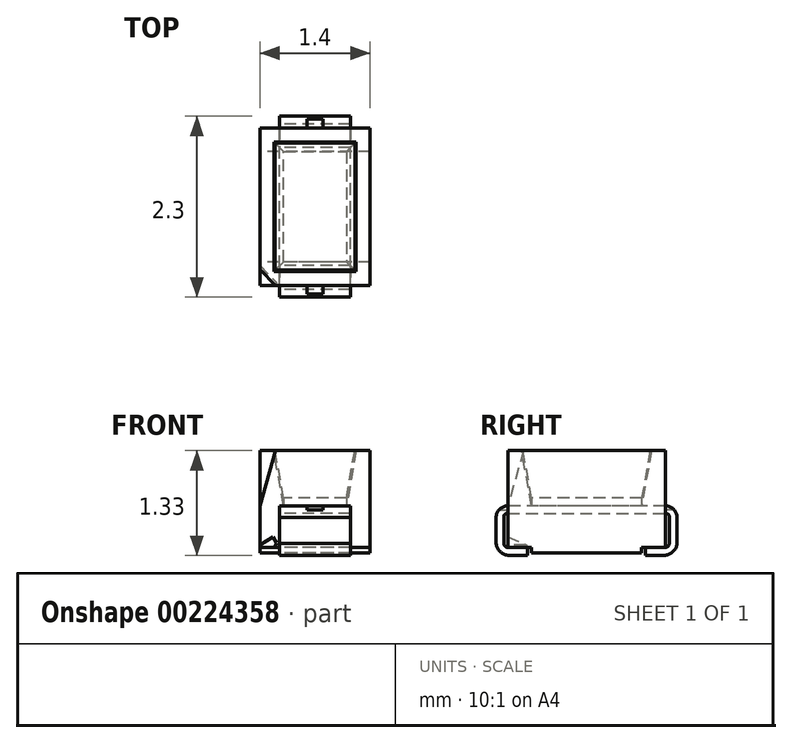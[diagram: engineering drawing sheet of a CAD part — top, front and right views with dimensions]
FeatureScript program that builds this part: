
annotation { "Feature Type Name" : "Feature", "Feature Type Description" : "" }
export const myFeature = defineFeature(function(context is Context, id is Id, definition is map)
    precondition{}
    {
        {
            var Q0;
            Q0=qCreatedBy(makeId("Top.planeOp"),FACE);
            var sketch = newSketch(context, id + "F0", { "sketchPlane" : qUnion([Q0])});
            skLineSegment(sketch, "E0.bottom", {"start": v(0.7, -1) * mm, "end": v(-0.7, -1) * mm});
            skLineSegment(sketch, "E0.top", {"start": v(0.7, 1) * mm, "end": v(-0.7, 1) * mm});
            skLineSegment(sketch, "E0.left", {"start": v(0.7, -1) * mm, "end": v(0.7, 1) * mm});
            skLineSegment(sketch, "E0.right", {"start": v(-0.7, -1) * mm, "end": v(-0.7, 1) * mm});
            skPoint(sketch, "E0.middle", {"position": v(0, 0) * mm});
            skLineSegment(sketch, "E1.bottom", {"start": v(0.4, -0.7) * mm, "end": v(-0.4, -0.7) * mm});
            skLineSegment(sketch, "E1.top", {"start": v(0.4, 0.7) * mm, "end": v(-0.4, 0.7) * mm});
            skLineSegment(sketch, "E1.left", {"start": v(0.4, -0.7) * mm, "end": v(0.4, 0.7) * mm});
            skLineSegment(sketch, "E1.right", {"start": v(-0.4, -0.7) * mm, "end": v(-0.4, 0.7) * mm});
            skLineSegment(sketch, "E2.bottom", {"start": v(0.15, -0.4) * mm, "end": v(-0.15, -0.4) * mm});
            skLineSegment(sketch, "E2.top", {"start": v(0.15, -0.1) * mm, "end": v(-0.15, -0.1) * mm});
            skLineSegment(sketch, "E2.left", {"start": v(0.15, -0.4) * mm, "end": v(0.15, -0.1) * mm});
            skLineSegment(sketch, "E2.right", {"start": v(-0.15, -0.4) * mm, "end": v(-0.15, -0.1) * mm});
            skPoint(sketch, "E2.middle", {"position": v(0, -0.25) * mm});
            skSolve(sketch);
        }
        {
            var Q0;
            Q0=makeQuery(id+"F0.imprint","IMPRINT",FACE,{"disambiguationData":[TD([[makeQuery(id+"F0.imprint","IMPRINT",EDGE,{"derivedFrom":sQuery(id+"F0.wireOp",EDGE,"E0.bottom")}),-1.0]])]});
            var Q1;
            {var subQ1=sQuery(id+"F0.wireOp",EDGE,"E0.top");Q1=makeQuery(id+"F0.imprint","IMPRINT",FACE,{"disambiguationData":[TD([[makeQuery(id+"F0.imprint","IMPRINT",EDGE,{"derivedFrom":subQ1}),1.0]])]});}
            extrude(context, id + "F1", {"entities" : qUnion([Q0, Q1]), "depth" : .7 * mm, "hasSecondDirection" : true, "secondDirectionOppositeDirection" : true, "secondDirectionDepth" : .6 * mm});
        }
        {
            var Q0;
            Q0=makeQuery(id+"F0.imprint","IMPRINT",FACE,{"disambiguationData":[TD([[makeQuery(id+"F0.imprint","IMPRINT",EDGE,{"derivedFrom":sQuery(id+"F0.wireOp",EDGE,"E1.bottom")}),-1.0]])]});
            var Q1;
            Q1=makeQuery(id+"F1.opExtrude","CAP_FACE",FACE,{"disambiguationData":[OSD([sQuery(id+"F0.wireOp",EDGE,"E0.bottom"),sQuery(id+"F0.wireOp",EDGE,"E0.top"),sQuery(id+"F0.wireOp",EDGE,"E0.left"),sQuery(id+"F0.wireOp",EDGE,"E0.right"),sQuery(id+"F0.wireOp",EDGE,"E1.bottom"),sQuery(id+"F0.wireOp",EDGE,"E1.top"),sQuery(id+"F0.wireOp",EDGE,"E1.left"),sQuery(id+"F0.wireOp",EDGE,"E1.right")])],"isStart":false});
            extrude(context, id + "F2", {"entities" : qUnion([Q0]), "operationType" : NewBodyOperationType.REMOVE, "endBound" : BoundingType.UP_TO_SURFACE, "endBoundEntityFace" : qUnion([Q1]), "depth" : 25 * mm, "hasDraft" : true, "draftAngle" : 10 * degree});
        }
        {
            var Q0;
            Q0=makeQuery(id+"F0.imprint","IMPRINT",FACE,{"disambiguationData":[TD([[makeQuery(id+"F0.imprint","IMPRINT",EDGE,{"derivedFrom":sQuery(id+"F0.wireOp",EDGE,"E2.bottom")}),-1.0]])]});
            extrude(context, id + "F3", {"entities" : qUnion([Q0]), "depth" : .1 * mm});
        }
        {
            var Q0;
            Q0=makeQuery(id+"F0.imprint","IMPRINT",FACE,{"disambiguationData":[TD([[makeQuery(id+"F0.imprint","IMPRINT",EDGE,{"derivedFrom":sQuery(id+"F0.wireOp",EDGE,"E1.bottom")}),-1.0]])]});
            var Q1;
            Q1=makeQuery(id+"F1.opExtrude","CAP_FACE",FACE,{"disambiguationData":[OSD([sQuery(id+"F0.wireOp",EDGE,"E0.bottom"),sQuery(id+"F0.wireOp",EDGE,"E0.top"),sQuery(id+"F0.wireOp",EDGE,"E0.left"),sQuery(id+"F0.wireOp",EDGE,"E0.right"),sQuery(id+"F0.wireOp",EDGE,"E1.bottom"),sQuery(id+"F0.wireOp",EDGE,"E1.top"),sQuery(id+"F0.wireOp",EDGE,"E1.left"),sQuery(id+"F0.wireOp",EDGE,"E1.right")])],"isStart":true});
            extrude(context, id + "F4", {"entities" : qUnion([Q0]), "operationType" : NewBodyOperationType.ADD, "endBound" : BoundingType.UP_TO_SURFACE, "oppositeDirection" : true, "endBoundEntityFace" : qUnion([Q1]), "depth" : 25 * mm});
        }
        {
            var Q0;
            Q0=makeQuery(id+"F0.imprint","IMPRINT",FACE,{"disambiguationData":[TD([[makeQuery(id+"F0.imprint","IMPRINT",EDGE,{"derivedFrom":sQuery(id+"F0.wireOp",EDGE,"E1.bottom")}),-1.0]])]});
            extrude(context, id + "F5", {"entities" : qUnion([Q0]), "depth" : .1 * mm});
        }
        {
            var Q0;
            Q0=makeQuery(id+"F0.imprint","IMPRINT",FACE,{"disambiguationData":[TD([[makeQuery(id+"F0.imprint","IMPRINT",EDGE,{"derivedFrom":sQuery(id+"F0.wireOp",EDGE,"E2.bottom")}),-1.0]])]});
            var Q1;
            {var subQ0=sQuery(id+"F0.wireOp",EDGE,"E1.right");var subQ1=sQuery(id+"F0.wireOp",EDGE,"E1.left");var subQ2=sQuery(id+"F0.wireOp",EDGE,"E1.top");var subQ3=sQuery(id+"F0.wireOp",EDGE,"E1.bottom");var subQ4=sQuery(id+"F0.wireOp",EDGE,"E0.right");var subQ5=sQuery(id+"F0.wireOp",EDGE,"E0.left");var subQ6=sQuery(id+"F0.wireOp",EDGE,"E0.top");var subQ7=sQuery(id+"F0.wireOp",EDGE,"E0.bottom");Q1=makeQuery(id+"F4.boolean.opBoolean","MERGE",FACE,{"derivedFrom":[makeQuery(id+"F1.opExtrude","CAP_FACE",FACE,{"disambiguationData":[OSD([subQ7,subQ6,subQ5,subQ4,subQ3,subQ2,subQ1,subQ0])],"isStart":true}),makeQuery(id+"F4.opExtrude","CAP_FACE",FACE,{"disambiguationData":[OSD([subQ7,subQ6,subQ5,subQ4,subQ3,subQ2,subQ1,subQ0])],"isStart":false})]});}
            extrude(context, id + "F6", {"entities" : qUnion([Q0]), "operationType" : NewBodyOperationType.ADD, "endBound" : BoundingType.UP_TO_SURFACE, "oppositeDirection" : true, "endBoundEntityFace" : qUnion([Q1]), "depth" : 25 * mm});
        }
        {
            var Q0;
            Q0=makeQuery(id+"F1.opExtrude","SWEPT_FACE",FACE,{"disambiguationData":[OSD([sQuery(id+"F0.wireOp",EDGE,"E0.right")])]});
            var sketch = newSketch(context, id + "F7", { "sketchPlane" : qUnion([Q0])});
            skLineSegment(sketch, "E3", {"start": v(-1, 0.7) * mm, "end": v(1, 0.7) * mm, "construction": true});
            skLineSegment(sketch, "E4", {"start": v(1, 0.7) * mm, "end": v(1, -0.6) * mm, "construction": true});
            skLineSegment(sketch, "E5", {"start": v(1, -0.6) * mm, "end": v(-1, -0.6) * mm, "construction": true});
            skLineSegment(sketch, "E6", {"start": v(-1, -0.6) * mm, "end": v(-1, 0.7) * mm, "construction": true});
            skLineSegment(sketch, "E7", {"start": v(-1.16, -0.53) * mm, "end": v(-0.7, -0.53) * mm});
            skLineSegment(sketch, "E8", {"start": v(-0.7, -0.53) * mm, "end": v(-0.7, -0.74) * mm});
            skLineSegment(sketch, "E9", {"start": v(-0.7, -0.74) * mm, "end": v(0.7, -0.74) * mm});
            skLineSegment(sketch, "E10", {"start": v(0.7, -0.74) * mm, "end": v(0.7, -0.53) * mm});
            skLineSegment(sketch, "E11", {"start": v(0.7, -0.53) * mm, "end": v(1.16, -0.53) * mm});
            skLineSegment(sketch, "E12", {"start": v(1.16, -0.53) * mm, "end": v(1.16, -0.97) * mm});
            skLineSegment(sketch, "E13", {"start": v(1.16, -0.97) * mm, "end": v(-1.16, -0.97) * mm});
            skLineSegment(sketch, "E14", {"start": v(-1.16, -0.97) * mm, "end": v(-1.16, -0.53) * mm});
            skSolve(sketch);
        }
        {
            var Q0;
            {var subQ0=sQuery(id+"F7.wireOp",EDGE,"E8");var subQ1=sQuery(id+"F7.wireOp",EDGE,"E7");var subQ2=makeQuery(id+"F7.imprint","INTERSECT",VERTEX,{"derivedFrom":[subQ1,subQ0]});Q0=makeQuery(id+"F7.imprint","IMPRINT",FACE,{"disambiguationData":[TD([[makeQuery(id+"F7.imprint","IMPRINT",EDGE,{"disambiguationData":[TD([[subQ2,-1.0]])],"derivedFrom":subQ0}),-1.0]])]});}
            var Q1;
            {var subQ0=sQuery(id+"F7.wireOp",EDGE,"E11");var subQ1=sQuery(id+"F7.wireOp",EDGE,"E10");var subQ2=makeQuery(id+"F7.imprint","INTERSECT",VERTEX,{"derivedFrom":[subQ1,subQ0]});Q1=makeQuery(id+"F7.imprint","IMPRINT",FACE,{"disambiguationData":[TD([[makeQuery(id+"F7.imprint","IMPRINT",EDGE,{"disambiguationData":[TD([[subQ2,1.0]])],"derivedFrom":subQ1}),-1.0]])]});}
            extrude(context, id + "F8", {"entities" : qUnion([Q0, Q1]), "operationType" : NewBodyOperationType.REMOVE, "endBound" : BoundingType.UP_TO_NEXT, "oppositeDirection" : true, "depth" : 25 * mm});
        }
        {
            var Q0;
            Q0=makeQuery(id+"F1.opExtrude","SWEPT_FACE",FACE,{"disambiguationData":[OSD([sQuery(id+"F0.wireOp",EDGE,"E0.right")])]});
            var sketch = newSketch(context, id + "F9", { "sketchPlane" : qUnion([Q0])});
            skLineSegment(sketch, "E15", {"start": v(-1, 0) * mm, "end": v(1, 0) * mm, "construction": true});
            skLineSegment(sketch, "E16", {"start": v(-1.15, -0.15) * mm, "end": v(-1.15, -0.48) * mm});
            skLineSegment(sketch, "E17", {"start": v(-1, -0.63) * mm, "end": v(-0.75, -0.63) * mm});
            skLineSegment(sketch, "E18", {"start": v(-1.15, 0) * mm, "end": v(1.15, 0) * mm});
            skLineSegment(sketch, "E19", {"start": v(1.15, -0.15) * mm, "end": v(1.15, -0.48) * mm});
            skLineSegment(sketch, "E20", {"start": v(1, -0.63) * mm, "end": v(0.75, -0.63) * mm});
            skLineSegment(sketch, "E21", {"start": v(0.75, -0.63) * mm, "end": v(0.75, -0.53) * mm});
            skLineSegment(sketch, "E22", {"start": v(0.75, -0.53) * mm, "end": v(1, -0.53) * mm});
            skLineSegment(sketch, "E23", {"start": v(1.05, -0.48) * mm, "end": v(1.05, -0.15) * mm});
            skLineSegment(sketch, "E24", {"start": v(1, -0.1) * mm, "end": v(-1, -0.1) * mm});
            skLineSegment(sketch, "E25", {"start": v(-1.05, -0.15) * mm, "end": v(-1.05, -0.48) * mm});
            skLineSegment(sketch, "E26", {"start": v(-1, -0.53) * mm, "end": v(-0.75, -0.53) * mm});
            skLineSegment(sketch, "E27", {"start": v(-0.75, -0.53) * mm, "end": v(-0.75, -0.63) * mm});
            skPoint(sketch, "E28.visualSharp", {"position": v(-1.05, -0.1) * mm});
            skArc(sketch, "E28.filletArc", {"start": v(-1, -0.1) * mm, "mid": v(-1.04, -0.11) * mm, "end": v(-1.05, -0.15) * mm});
            skPoint(sketch, "E29.newPointA", {"position": v(0, 0) * mm});
            skArc(sketch, "E29.filletArc", {"start": v(-1, 0) * mm, "mid": v(-1.1, -0.04) * mm, "end": v(-1.15, -0.15) * mm});
            skPoint(sketch, "E30.visualSharp", {"position": v(-1.15, -0.63) * mm});
            skArc(sketch, "E30.filletArc", {"start": v(-1.15, -0.48) * mm, "mid": v(-1.1, -0.58) * mm, "end": v(-1, -0.63) * mm});
            skPoint(sketch, "E31.visualSharp", {"position": v(-1.05, -0.53) * mm});
            skArc(sketch, "E31.filletArc", {"start": v(-1.05, -0.48) * mm, "mid": v(-1.04, -0.51) * mm, "end": v(-1, -0.53) * mm});
            skPoint(sketch, "E32.visualSharp", {"position": v(1.05, -0.53) * mm});
            skArc(sketch, "E32.filletArc", {"start": v(1, -0.53) * mm, "mid": v(1.04, -0.51) * mm, "end": v(1.05, -0.48) * mm});
            skPoint(sketch, "E33.visualSharp", {"position": v(1.05, -0.1) * mm});
            skArc(sketch, "E33.filletArc", {"start": v(1.05, -0.15) * mm, "mid": v(1.04, -0.11) * mm, "end": v(1, -0.1) * mm});
            skArc(sketch, "E34.filletArc", {"start": v(1.15, -0.15) * mm, "mid": v(1.1, -0.04) * mm, "end": v(1, 0) * mm});
            skPoint(sketch, "E35.visualSharp", {"position": v(1.15, -0.63) * mm});
            skArc(sketch, "E35.filletArc", {"start": v(1, -0.63) * mm, "mid": v(1.1, -0.58) * mm, "end": v(1.15, -0.48) * mm});
            skSolve(sketch);
        }
        {
            var Q0;
            Q0 = qSketchRegion(id + "F9", true);
            var Q1;
            Q1=makeQuery(id+"F1.opExtrude","SWEPT_FACE",FACE,{"disambiguationData":[OSD([sQuery(id+"F0.wireOp",EDGE,"E0.left")])]});
            extrude(context, id + "F10", {"entities" : qUnion([Q0]), "oppositeDirection" : true, "endBoundEntityFace" : qUnion([Q1]), "depth" : 1.15 * mm, "hasSecondDirection" : true, "secondDirectionOppositeDirection" : true, "secondDirectionDepth" : .25 * mm});
        }
        {
            var Q0;
            Q0=makeQuery(id+"F5.opExtrude","CAP_FACE",FACE,{"disambiguationData":[OSD([sQuery(id+"F0.wireOp",EDGE,"E1.bottom"),sQuery(id+"F0.wireOp",EDGE,"E1.top"),sQuery(id+"F0.wireOp",EDGE,"E1.left"),sQuery(id+"F0.wireOp",EDGE,"E1.right"),sQuery(id+"F0.wireOp",EDGE,"E2.bottom"),sQuery(id+"F0.wireOp",EDGE,"E2.top"),sQuery(id+"F0.wireOp",EDGE,"E2.left"),sQuery(id+"F0.wireOp",EDGE,"E2.right")])],"isStart":false});
            var sketch = newSketch(context, id + "F11", { "sketchPlane" : qUnion([Q0])});
            skLineSegment(sketch, "E36.0.1", {"start": v(-0.45, 1) * mm, "end": v(0.45, 1) * mm});
            skLineSegment(sketch, "E37", {"start": v(0, 1) * mm, "end": v(0.1, 1) * mm});
            skLineSegment(sketch, "E38", {"start": v(0.1, 1) * mm, "end": v(0.1, 1.2) * mm});
            skLineSegment(sketch, "E39", {"start": v(0.1, 1.2) * mm, "end": v(-0.1, 1.2) * mm});
            skLineSegment(sketch, "E40", {"start": v(-0.1, 1.2) * mm, "end": v(-0.1, 1) * mm});
            skLineSegment(sketch, "E41", {"start": v(-0.1, 1) * mm, "end": v(0, 1) * mm});
            skPoint(sketch, "E42.startSnap0", {"position": v(-0.15, -0.25) * mm});
            skPoint(sketch, "E36.0.2.end.orphan", {"position": v(0.45, 1.15) * mm});
            skPoint(sketch, "E36.0.0.start.orphan", {"position": v(-0.45, 1.15) * mm});
            skLineSegment(sketch, "E43", {"start": v(-0.78, 0) * mm, "end": v(1.2, 0) * mm, "construction": true});
            skLineSegment(sketch, "E44.MirrorCS", {"start": v(-0.1, -1) * mm, "end": v(0, -1) * mm});
            skLineSegment(sketch, "E45.MirrorCS", {"start": v(-0.1, -1.2) * mm, "end": v(-0.1, -1) * mm});
            skLineSegment(sketch, "E46.MirrorCS", {"start": v(0, -1) * mm, "end": v(0.1, -1) * mm});
            skLineSegment(sketch, "E47.MirrorCS", {"start": v(0.1, -1.2) * mm, "end": v(-0.1, -1.2) * mm});
            skLineSegment(sketch, "E48.MirrorCS", {"start": v(0.1, -1) * mm, "end": v(0.1, -1.2) * mm});
            skSolve(sketch);
        }
        {
            var Q0;
            Q0 = qSketchRegion(id + "F11", true);
            extrude(context, id + "F12", {"entities" : qUnion([Q0]), "operationType" : NewBodyOperationType.REMOVE, "oppositeDirection" : true, "depth" : .15 * mm});
        }
        {
            var Q0;
            Q0=makeQuery(id+"F1.opExtrude","SWEPT_FACE",FACE,{"disambiguationData":[OSD([sQuery(id+"F0.wireOp",EDGE,"E0.bottom")])]});
            var sketch = newSketch(context, id + "F13", { "sketchPlane" : qUnion([Q0])});
            skLineSegment(sketch, "E49", {"start": v(-0.7, 0) * mm, "end": v(-0.5, 0.7) * mm});
            skLineSegment(sketch, "E50", {"start": v(-0.7, -0.13) * mm, "end": v(-0.45, -0.53) * mm});
            skSolve(sketch);
        }
        {
            var Q0;
            Q0=makeQuery(id+"F1.opExtrude","SWEPT_FACE",FACE,{"disambiguationData":[OSD([sQuery(id+"F0.wireOp",EDGE,"E0.right")])]});
            var sketch = newSketch(context, id + "F14", { "sketchPlane" : qUnion([Q0])});
            skLineSegment(sketch, "E51", {"start": v(0.8, 0.7) * mm, "end": v(1, 0) * mm});
            skLineSegment(sketch, "E52", {"start": v(1, 0) * mm, "end": v(1, 0.7) * mm});
            skLineSegment(sketch, "E53", {"start": v(0.7, -0.53) * mm, "end": v(1, -0.53) * mm});
            skLineSegment(sketch, "E54", {"start": v(1, 0.7) * mm, "end": v(1, -0.53) * mm});
            skLineSegment(sketch, "E55", {"start": v(1, 0.7) * mm, "end": v(-1, 0.7) * mm});
            skLineSegment(sketch, "E56", {"start": v(-1, 0.7) * mm, "end": v(-1, -0.53) * mm});
            skLineSegment(sketch, "E57", {"start": v(-1, -0.53) * mm, "end": v(-0.7, -0.53) * mm});
            skLineSegment(sketch, "E58", {"start": v(-0.7, -0.53) * mm, "end": v(-0.7, -0.6) * mm});
            skLineSegment(sketch, "E59", {"start": v(0.7, -0.6) * mm, "end": v(-0.7, -0.6) * mm});
            skLineSegment(sketch, "E60", {"start": v(0.7, -0.6) * mm, "end": v(0.7, -0.53) * mm});
            skLineSegment(sketch, "E61", {"start": v(1, -0.13) * mm, "end": v(0.75, -0.53) * mm});
            skSolve(sketch);
        }
        {
            var Q0;
            Q0=makeQuery(id+"F1.opExtrude","CAP_FACE",FACE,{"disambiguationData":[OSD([sQuery(id+"F0.wireOp",EDGE,"E0.bottom"),sQuery(id+"F0.wireOp",EDGE,"E0.top"),sQuery(id+"F0.wireOp",EDGE,"E0.left"),sQuery(id+"F0.wireOp",EDGE,"E0.right"),sQuery(id+"F0.wireOp",EDGE,"E1.bottom"),sQuery(id+"F0.wireOp",EDGE,"E1.top"),sQuery(id+"F0.wireOp",EDGE,"E1.left"),sQuery(id+"F0.wireOp",EDGE,"E1.right")])],"isStart":false});
            var sketch = newSketch(context, id + "F15", { "sketchPlane" : qUnion([Q0])});
            skLineSegment(sketch, "E62", {"start": v(-0.7, -0.8) * mm, "end": v(-0.5, -1) * mm});
            skSolve(sketch);
        }
        {
            var Q0;
            Q0=sQuery(id+"F15.wireOp",VERTEX,"E62.start");
            var Q1;
            Q1=sQuery(id+"F15.wireOp",VERTEX,"E62.end");
            var Q2;
            Q2=sQuery(id+"F14.wireOp",VERTEX,"E52.start");
            cPlane(context, id + "F16", {"entities" : qUnion([Q0, Q1, Q2]), "cplaneType" : CPlaneType.THREE_POINT, "offset" : 25 * mm, "width" : 150 * mm, "height" : 150 * mm});
        }
        {
            var Q0;
            Q0=qCreatedBy(id+"F16.planeOp",FACE);
            var sketch = newSketch(context, id + "F17", { "sketchPlane" : qUnion([Q0])});
            skLineSegment(sketch, "E63.bottom", {"start": v(-0.04, 0.54) * mm, "end": v(0.57, 0.54) * mm});
            skLineSegment(sketch, "E63.top", {"start": v(-0.04, -0.39) * mm, "end": v(0.57, -0.39) * mm});
            skLineSegment(sketch, "E63.left", {"start": v(-0.04, 0.54) * mm, "end": v(-0.04, -0.39) * mm});
            skLineSegment(sketch, "E63.right", {"start": v(0.57, 0.54) * mm, "end": v(0.57, -0.39) * mm});
            skSolve(sketch);
        }
        {
            var Q0;
            Q0 = qSketchRegion(id + "F17", true);
            extrude(context, id + "F18", {"entities" : qUnion([Q0]), "operationType" : NewBodyOperationType.REMOVE, "endBound" : BoundingType.UP_TO_NEXT, "depth" : 25 * mm});
        }
        {
            var Q0;
            Q0=makeQuery(id+"F8.boolean.opBoolean","COPY",FACE,{"derivedFrom":makeQuery(id+"F8.opExtrude","SWEPT_FACE",FACE,{"disambiguationData":[OSD([sQuery(id+"F7.wireOp",EDGE,"E11")])]})});
            var sketch = newSketch(context, id + "F19", { "sketchPlane" : qUnion([Q0])});
            skLineSegment(sketch, "E64", {"start": v(-0.7, 0.75) * mm, "end": v(-0.45, 1) * mm});
            skSolve(sketch);
        }
        {
            var Q0;
            Q0=sQuery(id+"F19.wireOp",VERTEX,"E64.start");
            var Q1;
            Q1=sQuery(id+"F19.wireOp",VERTEX,"E64.end");
            var Q2;
            Q2=sQuery(id+"F14.wireOp",VERTEX,"E61.start");
            cPlane(context, id + "F20", {"entities" : qUnion([Q0, Q1, Q2]), "cplaneType" : CPlaneType.THREE_POINT, "offset" : 25 * mm, "width" : 150 * mm, "height" : 150 * mm});
        }
        {
            var Q0;
            Q0=qCreatedBy(id+"F20.planeOp",FACE);
            var sketch = newSketch(context, id + "F21", { "sketchPlane" : qUnion([Q0])});
            skLineSegment(sketch, "E65.0", {"start": v(-0.34, 0.26) * mm, "end": v(0, -0.07) * mm});
            skLineSegment(sketch, "E65.1", {"start": v(-0.34, 0.26) * mm, "end": v(-0.34, -0.2) * mm});
            skLineSegment(sketch, "E65.2", {"start": v(0, -0.07) * mm, "end": v(-0.34, -0.2) * mm});
            skSolve(sketch);
        }
        {
            var Q0;
            Q0 = qSketchRegion(id + "F21", true);
            extrude(context, id + "F22", {"entities" : qUnion([Q0]), "operationType" : NewBodyOperationType.REMOVE, "endBound" : BoundingType.THROUGH_ALL, "oppositeDirection" : true, "depth" : 25 * mm});
        }
        {
            var Q0;
            Q0=makeQuery(id+"F5.opExtrude","CAP_FACE",FACE,{"disambiguationData":[OSD([sQuery(id+"F0.wireOp",EDGE,"E1.bottom"),sQuery(id+"F0.wireOp",EDGE,"E1.top"),sQuery(id+"F0.wireOp",EDGE,"E1.left"),sQuery(id+"F0.wireOp",EDGE,"E1.right"),sQuery(id+"F0.wireOp",EDGE,"E2.bottom"),sQuery(id+"F0.wireOp",EDGE,"E2.top"),sQuery(id+"F0.wireOp",EDGE,"E2.left"),sQuery(id+"F0.wireOp",EDGE,"E2.right")])],"isStart":false});
            var sketch = newSketch(context, id + "F23", { "sketchPlane" : qUnion([Q0])});
            skLineSegment(sketch, "E66", {"start": v(-0.4, 0.7) * mm, "end": v(0.4, 0.7) * mm});
            skLineSegment(sketch, "E67", {"start": v(0.4, 0.7) * mm, "end": v(0.4, -0.7) * mm});
            skLineSegment(sketch, "E68", {"start": v(0.4, -0.7) * mm, "end": v(-0.4, -0.7) * mm});
            skLineSegment(sketch, "E69", {"start": v(-0.4, -0.7) * mm, "end": v(-0.4, 0.7) * mm});
            skSolve(sketch);
        }
        {
            var Q0;
            Q0 = qSketchRegion(id + "F23", true);
            var Q1;
            Q1=makeQuery(id+"F1.opExtrude","CAP_FACE",FACE,{"disambiguationData":[OSD([sQuery(id+"F0.wireOp",EDGE,"E0.bottom"),sQuery(id+"F0.wireOp",EDGE,"E0.top"),sQuery(id+"F0.wireOp",EDGE,"E0.left"),sQuery(id+"F0.wireOp",EDGE,"E0.right"),sQuery(id+"F0.wireOp",EDGE,"E1.bottom"),sQuery(id+"F0.wireOp",EDGE,"E1.top"),sQuery(id+"F0.wireOp",EDGE,"E1.left"),sQuery(id+"F0.wireOp",EDGE,"E1.right")])],"isStart":false});
            extrude(context, id + "F24", {"entities" : qUnion([Q0]), "endBound" : BoundingType.UP_TO_SURFACE, "endBoundEntityFace" : qUnion([Q1]), "depth" : 25 * mm, "hasDraft" : true, "draftAngle" : 10 * degree});
        }
    });
